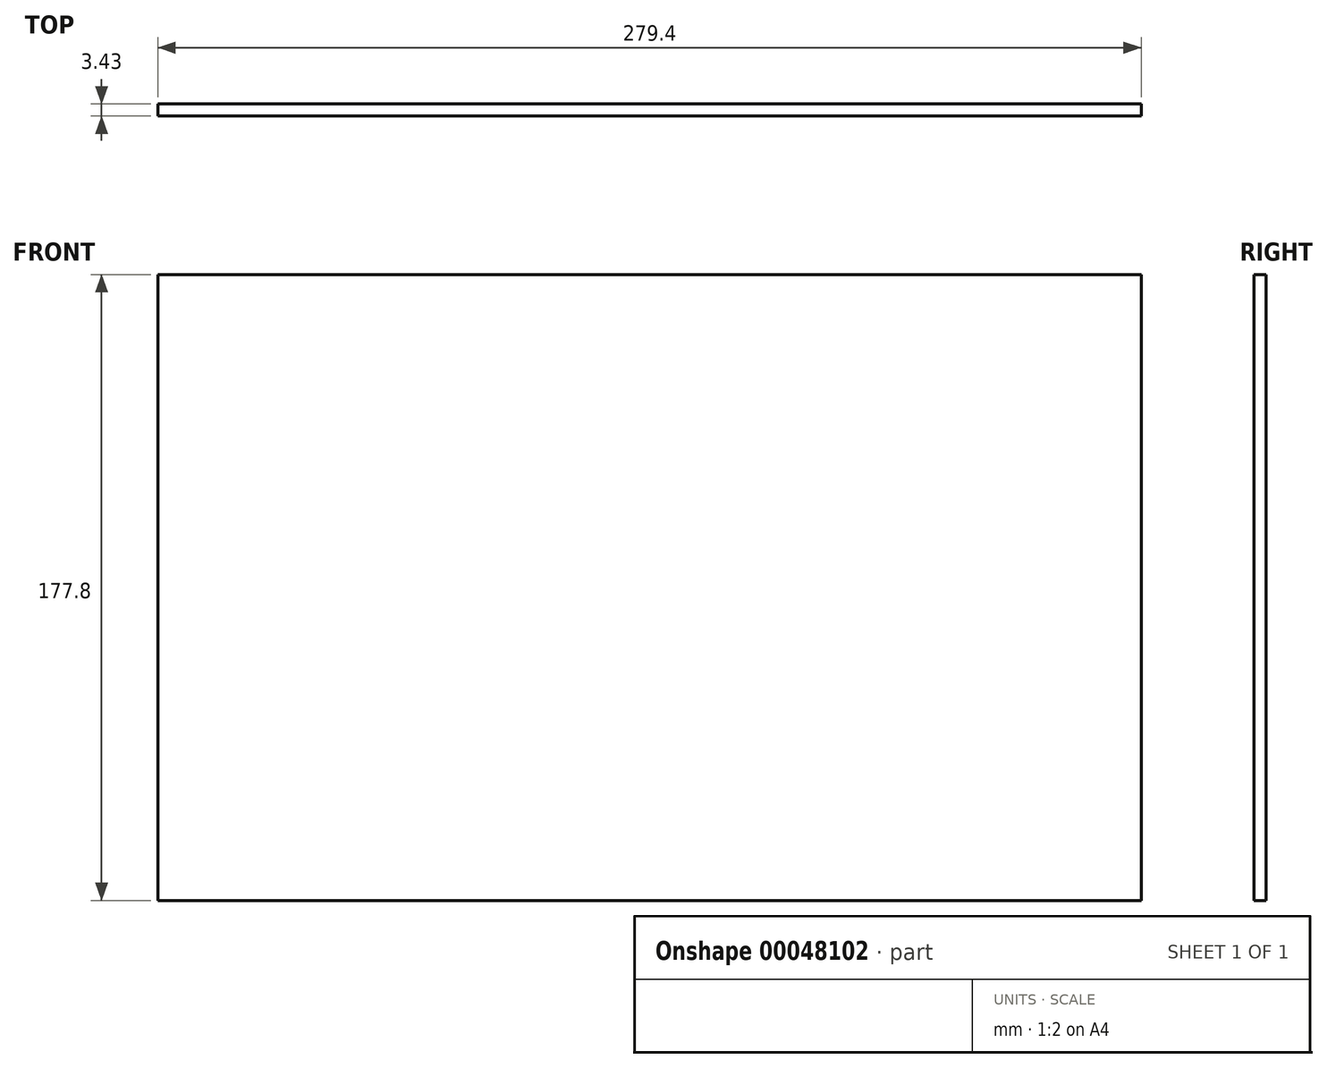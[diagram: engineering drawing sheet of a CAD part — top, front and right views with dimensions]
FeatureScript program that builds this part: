
annotation { "Feature Type Name" : "Feature", "Feature Type Description" : "" }
export const myFeature = defineFeature(function(context is Context, id is Id, definition is map)
    precondition{}
    {
        {
            var Q0;
            Q0=qCreatedBy(makeId("Front.planeOp"),FACE);
            var sketch = newSketch(context, id + "F0", { "sketchPlane" : qUnion([Q0])});
            skLineSegment(sketch, "E0.bottom", {"start": v(-139.7, 88.9) * mm, "end": v(139.7, 88.9) * mm});
            skLineSegment(sketch, "E0.top", {"start": v(-139.7, -88.9) * mm, "end": v(139.7, -88.9) * mm});
            skLineSegment(sketch, "E0.left", {"start": v(-139.7, 88.9) * mm, "end": v(-139.7, -88.9) * mm});
            skLineSegment(sketch, "E0.right", {"start": v(139.7, 88.9) * mm, "end": v(139.7, -88.9) * mm});
            skSolve(sketch);
        }
        {
            var Q0;
            Q0=makeQuery(id+"F0.imprint","IMPRINT",FACE,{"disambiguationData":[TD([[makeQuery(id+"F0.imprint","IMPRINT",EDGE,{"derivedFrom":sQuery(id+"F0.wireOp",EDGE,"E0.bottom")}),-1.0]])]});
            extrude(context, id + "F1", {"entities" : qUnion([Q0]), "depth" : 3.43 * mm});
        }
    });
